# Revit family: Articulating_Wall_Mount-Chief-JWS_Series
name_source: partatom
category: Specialty Equipment
revit_build: Autodesk Revit 2017 (Build: 20190508_0315(x64)
units: mm (PartAtom-declared; Revit-internal decimal feet)

## family parameters
Cut with Voids When Loaded = No
Host = Face
Part Type = Normal
Room Calculation Point = No
Round Connector Dimension = Use Diameter
Shared = No

## types (1)
- Medium, 12" Deep
    Date Modified = February 22, 2021
    Default Elevation = 48 "
    Description = Medium Flat Panel Single Arm Wall Display Mount - 12In. Extension
    Equipment Abbreviation = VM
    Family Version = 1.0
    Manufacturer = Chief
    Model = JWSUB
    Model Disclaimer = Contact Chief For More Information
    Part Description = Medium Flat Panel Single Arm Wall Display Mount - 12In. Extension
    Part Number = JWSUB
    Product Documentation Link = https://www.legrandav.com
    Product Page URL = https://www.legrandav.com
    URL = https://www.legrandav.com
    z Arm A Length = 8.5 "
    z Arm Pivot Elevation = 0 "
    z Arm Spacing End = 0 "
    z Arm Spacing Start = 0 "
    z Arm Thickness = 2 "
    z Arm Width = 1 "
    z Base Plate Arm Offset Height = 1 "
    z Base Plate Arm Offset Width = 0 "
    z Base Plate Height = 6.92 "
    z Base Plate Width = 3.22 "
    z Display Mount Elevation = 5.02 "
    z Display Mount Tilt Position Offset Depth = 0 "
    z Display Mount Tilt Position Offset Height = 0 "

## geometry (parser evidence)
native form markers: Sweep x18
no freeform markers — native parametric forms only
